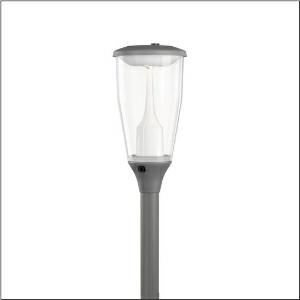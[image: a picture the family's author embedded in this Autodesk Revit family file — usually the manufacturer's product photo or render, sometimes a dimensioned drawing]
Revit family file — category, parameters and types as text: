
# Revit family: dl_11_iq___st1_2a_5xa5575ew14h000022_afae
name_source: partatom
category: Lighting Fixtures
units: mm (PartAtom-declared; Revit-internal decimal feet)

## family parameters
Cut with Voids When Loaded = No
Host = Face
Light Source = No
Part Type = Normal
Room Calculation Point = No
Round Connector Dimension = Use Diameter
Shared = No

## types (1)
- --- (1 x LED, 1560 lm, 10.7 W, 3000K)
    Apparent Load = 11 VA
    CIE Flux Codes = 24 63 94 96 100
    Color Rendering = 70
    Color Temperature = 3000K
    Default Elevation = 1800 mm
    Description = DL 11 iQ, mast luminaire, Module 540 iQ-SR, primary light control with 3 zone facetted reflector, of plastic, silver coated, highly specular, structured, primary optical cover: cover, of PMMA, transparent, light distribution: ST1.2a, light emission: direct distribution, primary light characteristic: asymmetric, installation type: post-top, LED, High Power LED, rated luminous flux: 1.560lm, luminous efficacy: 146lm/W, light colour: 730, colour temperature: 3000K, control gear: iQ-Street Remote, D4i with power reduction, control: pre-setting: logarithmic dimming characteristic, Street-Remote, Auto-Match, Temp-Guard, Lumen-Switch, Night-Set, Smart-Wire, Light-Fading, Desk-Remote (wireless, voltage-free reading and setting of iQ features in the workshop via application-optimized NFC function/RFID function), optimised constant luminous flux control (CLO 2.0), mains connection: 220..240V, AC, 50/60Hz, connection cable pre-assembled, cable length: 5,5m, start of lifetime: 11W, end of service life: 11W, reduction: 6W, luminaire housing, upper part, of diecast aluminium, coated, Siteco® metallic grey (DB 702S), spigot size: 76mm (post-top), mounting height: 3..5m, post-top mast mounting element, of diecast aluminium, coated, Siteco® metallic grey (DB 702S), Module 540 iQ-SR, traffic white (RAL 9016), equipment: standard, Smart Interface above and design motion detector below, protection rating (complete): IP65, insulation class (complete): insulation class II (safety insulation), certification: CE, ENEC, ENEC+, VDE, impact resistance: IK07, packaging unit: 1 piece

Light Distribution: ST1.2a
    Height = 665 mm
    Lamp = 1 x LED
    Lamp Light Flux = 1560 lm
    Lamp Power = 10.7 W
    Lamp count = 1
    Length = 334 mm
    Luminous efficacy = 146 lm/W
    Manufacturer = Siteco
    ModVariant = No
    Model = 5XA5575EW14H000022
    Number of Poles = 1
    OnlyDefault = Yes
    Power Factor = 1
    Product Name = DL 11 iQ | ST1.2a
    Product group = mast luminaire | pylon top
    ProductGroupID = 6100
    Protection Class = Protection class II
    Protection Degree = IP 65
    RLX_Detail_Level = 1
    RLX_Emergency_Light_Flux = 0 lm
    RLX_Emergency_Type = 0
    RLX_Emergency_Type_DB = No
    RlxData = <blob elided: 158697 chars, md5=7f656dec>
    Socket = socket
    Standby Power = 0 W
    System Light Flux = 1560 lm
    System Power = 11 W
    Type Comments = factory setting: luminous flux: 100 % | dim-lin: 254 | 419 mA
    Type Image = l_1337543.jpg
    URL = http://relux.com
    VarID = @adj_094688
    Voltage = 0 V
    Weight = 0.00 kg
    Width = 0 mm  [stored 0 ft]

note: [stored X ft] marks values corroborated as IEEE doubles in the binary element streams (Revit-internal decimal feet)

## geometry (parser evidence)
native form markers: Blend x4, Sweep x12
no freeform markers — native parametric forms only
